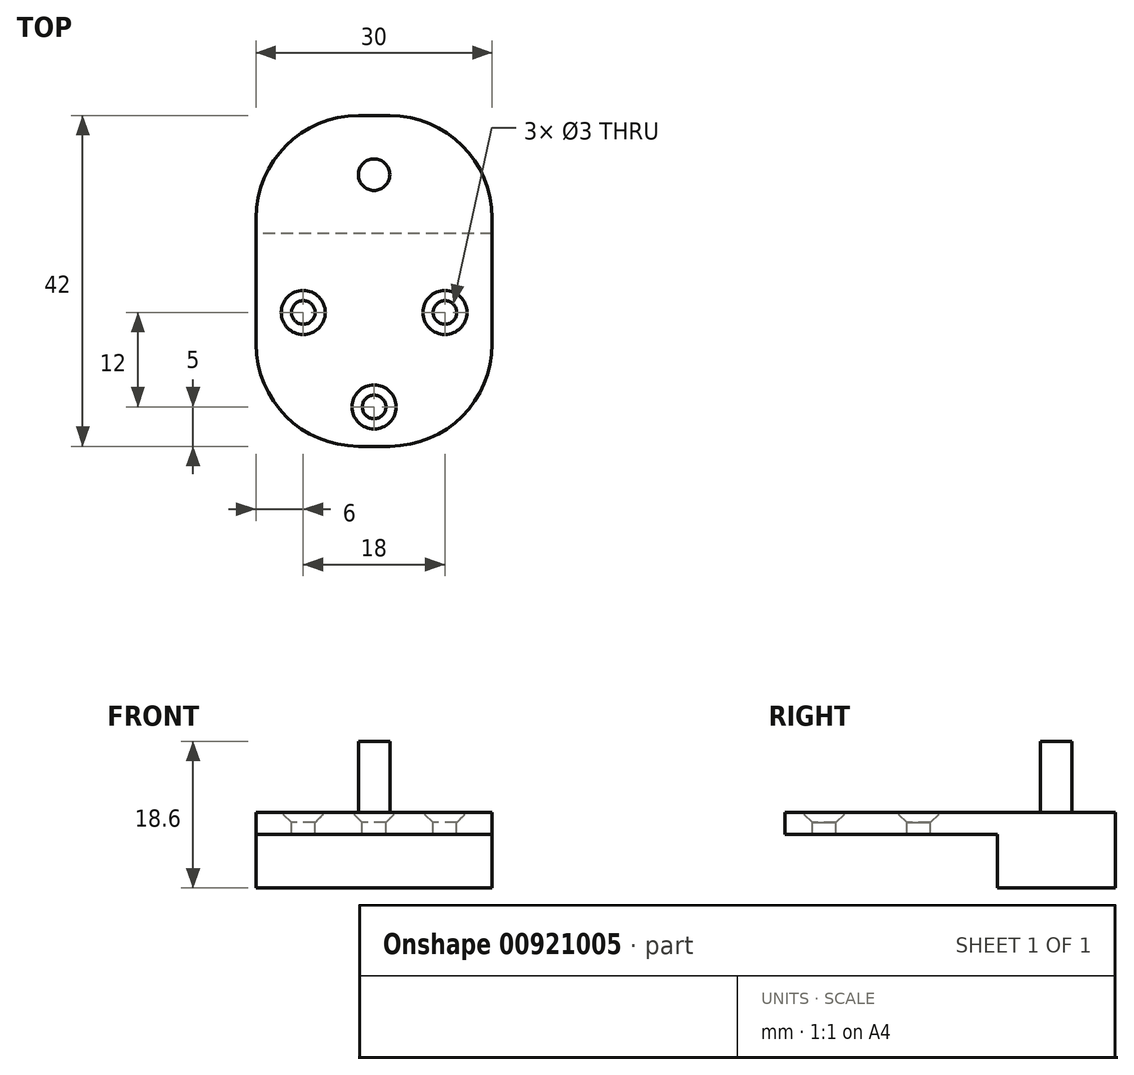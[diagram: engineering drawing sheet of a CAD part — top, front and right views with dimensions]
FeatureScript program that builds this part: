
annotation { "Feature Type Name" : "Feature", "Feature Type Description" : "" }
export const myFeature = defineFeature(function(context is Context, id is Id, definition is map)
    precondition{}
    {
        {
            var Q0;
            Q0=qCreatedBy(makeId("Right.planeOp"),FACE);
            var sketch = newSketch(context, id + "F0", { "sketchPlane" : qUnion([Q0])});
            skLineSegment(sketch, "E0", {"start": v(-27, 1.07) * mm, "end": v(15, 1.07) * mm});
            skLineSegment(sketch, "E1", {"start": v(15, 1.07) * mm, "end": v(15, -8.53) * mm});
            skLineSegment(sketch, "E2", {"start": v(15, -8.53) * mm, "end": v(0, -8.53) * mm});
            skLineSegment(sketch, "E3", {"start": v(0, -8.53) * mm, "end": v(0, -1.73) * mm});
            skLineSegment(sketch, "E4", {"start": v(0, -1.73) * mm, "end": v(-27, -1.73) * mm});
            skLineSegment(sketch, "E5", {"start": v(-27, -1.73) * mm, "end": v(-27, 1.07) * mm});
            skLineSegment(sketch, "E6", {"start": v(0, -1.73) * mm, "end": v(0, 1.07) * mm});
            skSolve(sketch);
        }
        {
            var Q0;
            {var subQ0=sQuery(id+"F0.wireOp",EDGE,"E1");Q0=makeQuery(id+"F0.imprint","IMPRINT",FACE,{"disambiguationData":[TD([[makeQuery(id+"F0.imprint","IMPRINT",EDGE,{"derivedFrom":subQ0}),-1.0]])]});}
            var Q1;
            Q1=makeQuery(id+"F0.imprint","IMPRINT",FACE,{"disambiguationData":[TD([[makeQuery(id+"F0.imprint","IMPRINT",EDGE,{"derivedFrom":sQuery(id+"F0.wireOp",EDGE,"E4")}),-1.0]])]});
            extrude(context, id + "F1", {"entities" : qUnion([Q0, Q1]), "endBound" : BoundingType.SYMMETRIC, "depth" : 30 * mm, "offsetDistance" : 25 * mm});
        }
        {
            var Q0;
            Q0=makeQuery(id+"F1.opExtrude","CAP_EDGE",EDGE,{"disambiguationData":[OSD([sQuery(id+"F0.wireOp",EDGE,"E1")])],"isStart":false});
            var Q1;
            Q1=makeQuery(id+"F1.opExtrude","CAP_EDGE",EDGE,{"disambiguationData":[OSD([sQuery(id+"F0.wireOp",EDGE,"E1")])],"isStart":true});
            fillet(context, id + "F2", {"entities" : qUnion([Q0, Q1]), "radius" : 13 * mm, "tangentPropagation" : true, "allowEdgeOverflow" : false});
        }
        {
            var Q0;
            Q0=makeQuery(id+"F1.opExtrude","CAP_EDGE",EDGE,{"disambiguationData":[OSD([sQuery(id+"F0.wireOp",EDGE,"E5")])],"isStart":false});
            var Q1;
            Q1=makeQuery(id+"F1.opExtrude","CAP_EDGE",EDGE,{"disambiguationData":[OSD([sQuery(id+"F0.wireOp",EDGE,"E5")])],"isStart":true});
            fillet(context, id + "F3", {"entities" : qUnion([Q0, Q1]), "radius" : 13 * mm, "tangentPropagation" : true, "allowEdgeOverflow" : false});
        }
        {
            var Q0;
            Q0=makeQuery(id+"F1.opExtrude","SWEPT_FACE",FACE,{"disambiguationData":[OSD([sQuery(id+"F0.wireOp",EDGE,"E0")])]});
            var sketch = newSketch(context, id + "F4", { "sketchPlane" : qUnion([Q0])});
            skPoint(sketch, "E7", {"position": v(-9, -10) * mm});
            skPoint(sketch, "E8", {"position": v(9, -10) * mm});
            skPoint(sketch, "E9", {"position": v(0, -22) * mm});
            skLineSegment(sketch, "E10", {"start": v(-15, 0) * mm, "end": v(15, 0) * mm});
            skSolve(sketch);
        }
        {
            var Q0;
            Q0=sQuery(id+"F4.wireOp",VERTEX,"E7");
            var Q1;
            Q1=makeQuery(id+"F1.opExtrude","SWEPT_BODY",BODY,{"disambiguationData":[OSD([sQuery(id+"F0.wireOp",EDGE,"E0"),sQuery(id+"F0.wireOp",EDGE,"E1"),sQuery(id+"F0.wireOp",EDGE,"E2"),sQuery(id+"F0.wireOp",EDGE,"E3"),sQuery(id+"F0.wireOp",EDGE,"E4"),sQuery(id+"F0.wireOp",EDGE,"E5")])]});
            hole(context, id + "F5", {"style" : HoleStyle.C_SINK, "endStyle" : HoleEndStyle.THROUGH, "holeDiameter" : 3 * mm, "cSinkDiameter" : 5.6 * mm, "cSinkAngle" : 90 * degree, "majorDiameter" : 5 * mm, "isTappedThrough" : true, "tappedDepth" : 12 * mm, "tapClearance" : 3, "locations" : qUnion([Q0]), "scope" : qUnion([Q1])});
        }
        {
            var Q0;
            Q0=sQuery(id+"F4.wireOp",VERTEX,"E8");
            var Q1;
            Q1=makeQuery(id+"F1.opExtrude","SWEPT_BODY",BODY,{"disambiguationData":[OSD([sQuery(id+"F0.wireOp",EDGE,"E0"),sQuery(id+"F0.wireOp",EDGE,"E1"),sQuery(id+"F0.wireOp",EDGE,"E2"),sQuery(id+"F0.wireOp",EDGE,"E3"),sQuery(id+"F0.wireOp",EDGE,"E4"),sQuery(id+"F0.wireOp",EDGE,"E5")])]});
            hole(context, id + "F6", {"style" : HoleStyle.C_SINK, "endStyle" : HoleEndStyle.THROUGH, "holeDiameter" : 3 * mm, "cSinkDiameter" : 5.6 * mm, "cSinkAngle" : 90 * degree, "majorDiameter" : 5 * mm, "isTappedThrough" : true, "tappedDepth" : 12 * mm, "tapClearance" : 3, "locations" : qUnion([Q0]), "scope" : qUnion([Q1])});
        }
        {
            var Q0;
            Q0=sQuery(id+"F4.wireOp",VERTEX,"E9");
            var Q1;
            Q1=makeQuery(id+"F1.opExtrude","SWEPT_BODY",BODY,{"disambiguationData":[OSD([sQuery(id+"F0.wireOp",EDGE,"E0"),sQuery(id+"F0.wireOp",EDGE,"E1"),sQuery(id+"F0.wireOp",EDGE,"E2"),sQuery(id+"F0.wireOp",EDGE,"E3"),sQuery(id+"F0.wireOp",EDGE,"E4"),sQuery(id+"F0.wireOp",EDGE,"E5")])]});
            hole(context, id + "F7", {"style" : HoleStyle.C_SINK, "endStyle" : HoleEndStyle.THROUGH, "holeDiameter" : 3 * mm, "cSinkDiameter" : 5.6 * mm, "cSinkAngle" : 90 * degree, "majorDiameter" : 5 * mm, "isTappedThrough" : true, "tappedDepth" : 12 * mm, "tapClearance" : 3, "locations" : qUnion([Q0]), "scope" : qUnion([Q1])});
        }
        {
            var Q0;
            {var subQ5=sQuery(id+"F4.wireOp",EDGE,"E10");Q0=makeQuery(id+"F4.imprint","IMPRINT",FACE,{"disambiguationData":[TD([[makeQuery(id+"F4.imprint","IMPRINT",EDGE,{"derivedFrom":subQ5}),1.0]])]});}
            var sketch = newSketch(context, id + "F8", { "sketchPlane" : qUnion([Q0])});
            skCircle(sketch, "E11", {"center": v(0, 7.5) * mm, "radius": 2 * mm});
            skSolve(sketch);
        }
        {
            var Q0;
            Q0=makeQuery(id+"F8.imprint","IMPRINT",FACE,{"disambiguationData":[TD([[makeQuery(id+"F8.imprint","IMPRINT",EDGE,{"derivedFrom":sQuery(id+"F8.wireOp",EDGE,"E11")}),1.0]])]});
            extrude(context, id + "F9", {"entities" : qUnion([Q0]), "operationType" : NewBodyOperationType.ADD, "endBound" : BoundingType.SYMMETRIC, "depth" : 18 * mm, "offsetDistance" : 25 * mm});
        }
    });
